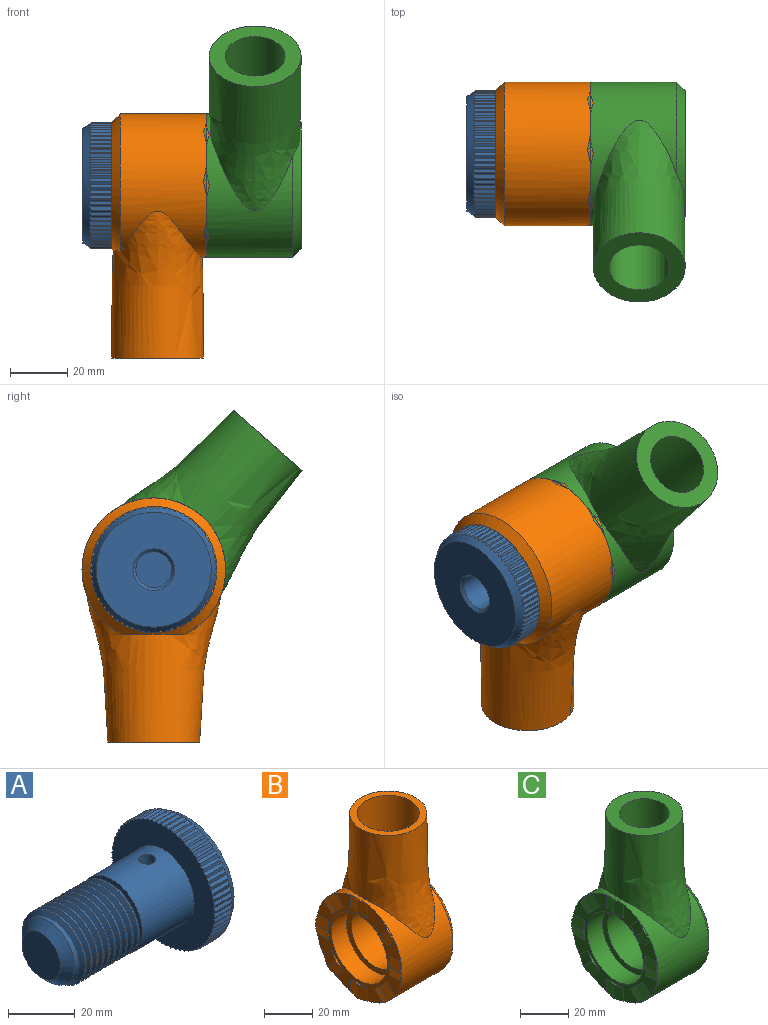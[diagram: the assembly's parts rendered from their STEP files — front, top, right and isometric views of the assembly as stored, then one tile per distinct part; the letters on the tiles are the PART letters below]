
ASSEMBLY  parts=3 mates=2
PART A: 232 faces, bbox 63x45x45 mm
  f0: cylinder r=13mm len=26mm, axis (1,0,0), area 1757.7mm2, adj f223,f224,f230,f231
  f1: cylinder r=6.25mm len=24mm, axis (1,0,0), area 902.3mm2, adj f228,f229,f230,f231
  f2: plane 1.59x1.25mm, normal (0,0,1), area 1.2mm2, adj f4,f6,f17,f224
  f3: bspline ~30.76x26.64mm, area 1329.7mm2, adj f4,f5,f8,f9,f10,f11,f12,f13
  f4: cylinder r=12.75mm len=25.5mm, axis (-1,0,0), area 454mm2, adj f2,f3,f5,f6,f224
  f5: plane 2.49x1.59mm, normal (0,0,-1), area 2.5mm2, adj f3,f4,f6,f7
  f6: bspline ~30.76x26.64mm, area 1376.2mm2, adj f2,f4,f5,f7,f8,f9,f10,f11
  f7: cylinder r=11.16mm len=22.33mm, axis (1,0,0), area 140.6mm2, adj f5,f6,f8,f19
  f8: cylinder r=11.16mm len=22.33mm, axis (1,0,0), area 0.7mm2, adj f3,f6,f7,f9
  f9: cylinder r=11.16mm len=22.33mm, axis (1,0,0), area 0.7mm2, adj f3,f6,f8,f10
  f10: cylinder r=11.16mm len=22.33mm, axis (1,0,0), area 0.8mm2, adj f3,f6,f9,f11
  f11: cylinder r=11.16mm len=22.33mm, axis (1,0,0), area 0.7mm2, adj f3,f6,f10,f12
  f12: cylinder r=11.16mm len=22.33mm, axis (1,0,0), area 0.7mm2, adj f3,f6,f11,f13
  f13: cylinder r=11.16mm len=22.33mm, axis (1,0,0), area 0.6mm2, adj f3,f6,f12,f14
  f14: cylinder r=11.16mm len=22.33mm, axis (1,0,0), area 0.8mm2, adj f3,f6,f13,f15
  f15: cylinder r=11.16mm len=22.33mm, axis (1,0,0), area 0.7mm2, adj f3,f6,f14,f16
  f16: cylinder r=11.16mm len=22.33mm, axis (1,0,0), area 0.7mm2, adj f3,f6,f15,f17
  f17: cylinder r=11.16mm len=22.33mm, axis (1,0,0), area 22.1mm2, adj f2,f3,f16,f224
  f18: plane 16.33x16.33mm, normal (-1,0,0), area 209.4mm2, adj f19
  f19: cone r=11.16mm half-angle=45deg, axis (1,0,0), area 257.6mm2, adj f7,f18
  f20: cylinder r=22mm len=7mm, axis (-1,0,0), area 0.2mm2, adj f21,f223,f225,f227
  f21: plane 7.81x0.97mm, normal (0,0.85,0.53), area 8.3mm2, adj f20,f22,f223,f225
  f22: plane 7.81x1.07mm, normal (0,0.93,-0.36), area 8.3mm2, adj f21,f23,f223,f225
  f23: cylinder r=22mm len=7mm, axis (-1,0,0), area 0.2mm2, adj f22,f24,f223,f225
  f24: plane 7.81x0.91mm, normal (0,0.8,0.6), area 8.3mm2, adj f23,f25,f223,f225
  f25: plane 7.81x1.1mm, normal (0,0.96,-0.28), area 8.3mm2, adj f24,f26,f223,f225
  f26: cylinder r=22mm len=7mm, axis (-1,0,0), area 0.2mm2, adj f25,f27,f223,f225
  f27: plane 7.81x0.85mm, normal (0,0.74,0.67), area 8.3mm2, adj f26,f28,f223,f225
  f28: plane 7.81x1.12mm, normal (0,0.98,-0.19), area 8.3mm2, adj f27,f29,f223,f225
  f29: cylinder r=22mm len=7mm, axis (-1,0,0), area 0.2mm2, adj f28,f30,f223,f225
  f30: plane 7.81x0.85mm, normal (0,0.67,0.74), area 8.3mm2, adj f29,f31,f223,f225
  f31: plane 7.81x1.14mm, normal (0,1,-0.09), area 8.3mm2, adj f30,f32,f223,f225
  f32: cylinder r=22mm len=7mm, axis (-1,0,0), area 0.2mm2, adj f31,f33,f223,f225
  f33: plane 7.81x0.92mm, normal (0,0.6,0.8), area 8.3mm2, adj f32,f34,f223,f225
  f34: plane 7.81x1.14mm, normal (0,1,0), area 8.3mm2, adj f33,f35,f223,f225
  f35: cylinder r=22mm len=7mm, axis (-1,0,0), area 0.2mm2, adj f34,f36,f223,f225
  f36: plane 7.81x0.98mm, normal (0,0.53,0.85), area 8.3mm2, adj f35,f37,f223,f225
  f37: plane 7.81x1.14mm, normal (0,1,0.09), area 8.3mm2, adj f36,f38,f223,f225
  f38: cylinder r=22mm len=7mm, axis (-1,0,0), area 0.2mm2, adj f37,f39,f223,f225
  f39: plane 7.81x1.03mm, normal (0,0.44,0.9), area 8.3mm2, adj f38,f40,f223,f225
  f40: plane 7.81x1.12mm, normal (0,0.98,0.18), area 8.3mm2, adj f39,f41,f223,f225
  f41: cylinder r=22mm len=7mm, axis (-1,0,0), area 0.2mm2, adj f40,f42,f223,f225
  f42: plane 7.81x1.07mm, normal (0,0.36,0.93), area 8.3mm2, adj f41,f43,f223,f225
  f43: plane 7.81x1.1mm, normal (0,0.96,0.27), area 8.3mm2, adj f42,f44,f223,f225
  f44: cylinder r=22mm len=7mm, axis (-1,0,0), area 0.2mm2, adj f43,f45,f223,f225
  f45: plane 7.81x1.1mm, normal (0,0.27,0.96), area 8.3mm2, adj f44,f46,f223,f225
  f46: plane 7.81x1.07mm, normal (0,0.93,0.36), area 8.3mm2, adj f45,f47,f223,f225
  f47: cylinder r=22mm len=7mm, axis (-1,0,0), area 0.2mm2, adj f46,f48,f223,f225
  f48: plane 7.81x1.12mm, normal (0,0.18,0.98), area 8.3mm2, adj f47,f49,f223,f225
  f49: plane 7.81x1.03mm, normal (0,0.9,0.44), area 8.3mm2, adj f48,f50,f223,f225
  f50: cylinder r=22mm len=7mm, axis (-1,0,0), area 0.2mm2, adj f49,f51,f223,f225
  f51: plane 7.81x1.14mm, normal (0,0.09,1), area 8.3mm2, adj f50,f52,f223,f225
  f52: plane 7.81x0.98mm, normal (0,0.85,0.53), area 8.3mm2, adj f51,f53,f223,f225
  f53: cylinder r=22mm len=7mm, axis (-1,0,0), area 0.2mm2, adj f52,f54,f223,f225
  f54: plane 7.81x1.14mm, normal (0,0,1), area 8.3mm2, adj f53,f55,f223,f225
  f55: plane 7.81x0.92mm, normal (0,0.8,0.6), area 8.3mm2, adj f54,f56,f223,f225
  f56: cylinder r=22mm len=7mm, axis (-1,0,0), area 0.2mm2, adj f55,f57,f223,f225
  f57: plane 7.81x1.14mm, normal (0,-0.09,1), area 8.3mm2, adj f56,f58,f223,f225
  f58: plane 7.81x0.85mm, normal (0,0.74,0.67), area 8.3mm2, adj f57,f59,f223,f225
  f59: cylinder r=22mm len=7mm, axis (-1,0,0), area 0.2mm2, adj f58,f60,f223,f225
  f60: plane 7.81x1.12mm, normal (0,-0.19,0.98), area 8.3mm2, adj f59,f61,f223,f225
  f61: plane 7.81x0.85mm, normal (0,0.67,0.74), area 8.3mm2, adj f60,f62,f223,f225
  f62: cylinder r=22mm len=7mm, axis (-1,0,0), area 0.2mm2, adj f61,f63,f223,f225
  f63: plane 7.81x1.1mm, normal (0,-0.28,0.96), area 8.3mm2, adj f62,f64,f223,f225
  f64: plane 7.81x0.91mm, normal (0,0.6,0.8), area 8.3mm2, adj f63,f65,f223,f225
  f65: cylinder r=22mm len=7mm, axis (-1,0,0), area 0.2mm2, adj f64,f66,f223,f225
  f66: plane 7.81x1.07mm, normal (0,-0.36,0.93), area 8.3mm2, adj f65,f67,f223,f225
  f67: plane 7.81x0.97mm, normal (0,0.53,0.85), area 8.3mm2, adj f66,f68,f223,f225
  f68: cylinder r=22mm len=7mm, axis (-1,0,0), area 0.2mm2, adj f67,f69,f223,f225
  f69: plane 7.81x1.02mm, normal (0,-0.45,0.89), area 8.3mm2, adj f68,f70,f223,f225
  f70: plane 7.81x1.02mm, normal (0,0.45,0.89), area 8.3mm2, adj f69,f71,f223,f225
  f71: cylinder r=22mm len=7mm, axis (-1,0,0), area 0.2mm2, adj f70,f72,f223,f225
  f72: plane 7.81x0.97mm, normal (0,-0.53,0.85), area 8.3mm2, adj f71,f73,f223,f225
  f73: plane 7.81x1.07mm, normal (0,0.36,0.93), area 8.3mm2, adj f72,f74,f223,f225
  f74: cylinder r=22mm len=7mm, axis (-1,0,0), area 0.2mm2, adj f73,f75,f223,f225
  f75: plane 7.81x0.91mm, normal (0,-0.6,0.8), area 8.3mm2, adj f74,f76,f223,f225
  f76: plane 7.81x1.1mm, normal (0,0.28,0.96), area 8.3mm2, adj f75,f77,f223,f225
  f77: cylinder r=22mm len=7mm, axis (-1,0,0), area 0.2mm2, adj f76,f78,f223,f225
  f78: plane 7.81x0.85mm, normal (0,-0.67,0.74), area 8.3mm2, adj f77,f79,f223,f225
  f79: plane 7.81x1.12mm, normal (0,0.19,0.98), area 8.3mm2, adj f78,f80,f223,f225
  f80: cylinder r=22mm len=7mm, axis (-1,0,0), area 0.2mm2, adj f79,f81,f223,f225
  f81: plane 7.81x0.85mm, normal (0,-0.74,0.67), area 8.3mm2, adj f80,f82,f223,f225
  f82: plane 7.81x1.14mm, normal (0,0.09,1), area 8.3mm2, adj f81,f83,f223,f225
  f83: cylinder r=22mm len=7mm, axis (-1,0,0), area 0.2mm2, adj f82,f84,f223,f225
  f84: plane 7.81x0.92mm, normal (0,-0.8,0.6), area 8.3mm2, adj f83,f85,f223,f225
  f85: plane 7.81x1.14mm, normal (0,0,1), area 8.3mm2, adj f84,f86,f223,f225
  f86: cylinder r=22mm len=7mm, axis (-1,0,0), area 0.2mm2, adj f85,f87,f223,f225
  f87: plane 7.81x0.98mm, normal (0,-0.85,0.53), area 8.3mm2, adj f86,f88,f223,f225
  f88: plane 7.81x1.14mm, normal (0,-0.09,1), area 8.3mm2, adj f87,f89,f223,f225
  f89: cylinder r=22mm len=7mm, axis (-1,0,0), area 0.2mm2, adj f88,f90,f223,f225
  f90: plane 7.81x1.03mm, normal (0,-0.9,0.44), area 8.3mm2, adj f89,f91,f223,f225
  f91: plane 7.81x1.12mm, normal (0,-0.18,0.98), area 8.3mm2, adj f90,f92,f223,f225
  f92: cylinder r=22mm len=7mm, axis (-1,0,0), area 0.2mm2, adj f91,f93,f223,f225
  f93: plane 7.81x1.07mm, normal (0,-0.93,0.36), area 8.3mm2, adj f92,f94,f223,f225
  f94: plane 7.81x1.1mm, normal (0,-0.27,0.96), area 8.3mm2, adj f93,f95,f223,f225
  f95: cylinder r=22mm len=7mm, axis (-1,0,0), area 0.2mm2, adj f94,f96,f223,f225
  f96: plane 7.81x1.1mm, normal (0,-0.96,0.27), area 8.3mm2, adj f95,f97,f223,f225
  f97: plane 7.81x1.07mm, normal (0,-0.36,0.93), area 8.3mm2, adj f96,f98,f223,f225
  f98: cylinder r=22mm len=7mm, axis (-1,0,0), area 0.2mm2, adj f97,f99,f223,f225
  f99: plane 7.81x1.12mm, normal (0,-0.98,0.18), area 8.3mm2, adj f98,f100,f223,f225
  f100: plane 7.81x1.03mm, normal (0,-0.44,0.9), area 8.3mm2, adj f99,f101,f223,f225
  f101: cylinder r=22mm len=7mm, axis (-1,0,0), area 0.2mm2, adj f100,f102,f223,f225
  f102: plane 7.81x1.14mm, normal (0,-1,0.09), area 8.3mm2, adj f101,f103,f223,f225
  f103: plane 7.81x0.98mm, normal (0,-0.53,0.85), area 8.3mm2, adj f102,f104,f223,f225
  f104: cylinder r=22mm len=7mm, axis (-1,0,0), area 0.2mm2, adj f103,f105,f223,f225
  f105: plane 7.81x1.14mm, normal (0,-1,0), area 8.3mm2, adj f104,f106,f223,f225
  f106: plane 7.81x0.92mm, normal (0,-0.6,0.8), area 8.3mm2, adj f105,f107,f223,f225
  f107: cylinder r=22mm len=7mm, axis (-1,0,0), area 0.2mm2, adj f106,f108,f223,f225
  f108: plane 7.81x1.14mm, normal (0,-1,-0.09), area 8.3mm2, adj f107,f109,f223,f225
  f109: plane 7.81x0.85mm, normal (0,-0.67,0.74), area 8.3mm2, adj f108,f110,f223,f225
  f110: cylinder r=22mm len=7mm, axis (-1,0,0), area 0.2mm2, adj f109,f111,f223,f225
  f111: plane 7.81x1.12mm, normal (0,-0.98,-0.19), area 8.3mm2, adj f110,f112,f223,f225
  f112: plane 7.81x0.85mm, normal (0,-0.74,0.67), area 8.3mm2, adj f111,f113,f223,f225
  f113: cylinder r=22mm len=7mm, axis (-1,0,0), area 0.2mm2, adj f112,f114,f223,f225
  f114: plane 7.81x1.1mm, normal (0,-0.96,-0.28), area 8.3mm2, adj f113,f115,f223,f225
  f115: plane 7.81x0.91mm, normal (0,-0.8,0.6), area 8.3mm2, adj f114,f116,f223,f225
  f116: cylinder r=22mm len=7mm, axis (-1,0,0), area 0.2mm2, adj f115,f117,f223,f225
  f117: plane 7.81x1.07mm, normal (0,-0.93,-0.36), area 8.3mm2, adj f116,f118,f223,f225
  f118: plane 7.81x0.97mm, normal (0,-0.85,0.53), area 8.3mm2, adj f117,f119,f223,f225
  f119: cylinder r=22mm len=7mm, axis (-1,0,0), area 0.2mm2, adj f118,f120,f223,f225
  f120: plane 7.81x1.02mm, normal (0,-0.89,-0.45), area 8.3mm2, adj f119,f121,f223,f225
  f121: plane 7.81x1.02mm, normal (0,-0.89,0.45), area 8.3mm2, adj f120,f122,f223,f225
  f122: cylinder r=22mm len=7mm, axis (-1,0,0), area 0.2mm2, adj f121,f123,f223,f225
  f123: plane 7.81x0.97mm, normal (0,-0.85,-0.53), area 8.3mm2, adj f122,f124,f223,f225
  f124: plane 7.81x1.07mm, normal (0,-0.93,0.36), area 8.3mm2, adj f123,f125,f223,f225
  f125: cylinder r=22mm len=7mm, axis (-1,0,0), area 0.2mm2, adj f124,f126,f223,f225
  f126: plane 7.81x0.91mm, normal (0,-0.8,-0.6), area 8.3mm2, adj f125,f127,f223,f225
  f127: plane 7.81x1.1mm, normal (0,-0.96,0.28), area 8.3mm2, adj f126,f128,f223,f225
  f128: cylinder r=22mm len=7mm, axis (-1,0,0), area 0.2mm2, adj f127,f129,f223,f225
  f129: plane 7.81x0.85mm, normal (0,-0.74,-0.67), area 8.3mm2, adj f128,f130,f223,f225
  f130: plane 7.81x1.12mm, normal (0,-0.98,0.19), area 8.3mm2, adj f129,f131,f223,f225
  f131: cylinder r=22mm len=7mm, axis (-1,0,0), area 0.2mm2, adj f130,f132,f223,f225
  f132: plane 7.81x0.85mm, normal (0,-0.67,-0.74), area 8.3mm2, adj f131,f133,f223,f225
  f133: plane 7.81x1.14mm, normal (0,-1,0.09), area 8.3mm2, adj f132,f134,f223,f225
  f134: cylinder r=22mm len=7mm, axis (-1,0,0), area 0.2mm2, adj f133,f135,f223,f225
  f135: plane 7.81x0.92mm, normal (0,-0.6,-0.8), area 8.3mm2, adj f134,f136,f223,f225
  f136: plane 7.81x1.14mm, normal (0,-1,0), area 8.3mm2, adj f135,f137,f223,f225
  f137: cylinder r=22mm len=7mm, axis (-1,0,0), area 0.2mm2, adj f136,f138,f223,f225
  f138: plane 7.81x0.98mm, normal (0,-0.53,-0.85), area 8.3mm2, adj f137,f139,f223,f225
  f139: plane 7.81x1.14mm, normal (0,-1,-0.09), area 8.3mm2, adj f138,f140,f223,f225
  f140: cylinder r=22mm len=7mm, axis (-1,0,0), area 0.2mm2, adj f139,f141,f223,f225
  f141: plane 7.81x1.03mm, normal (0,-0.44,-0.9), area 8.3mm2, adj f140,f142,f223,f225
  f142: plane 7.81x1.12mm, normal (0,-0.98,-0.18), area 8.3mm2, adj f141,f143,f223,f225
  f143: cylinder r=22mm len=7mm, axis (-1,0,0), area 0.2mm2, adj f142,f144,f223,f225
  f144: plane 7.81x1.07mm, normal (0,-0.36,-0.93), area 8.3mm2, adj f143,f145,f223,f225
  f145: plane 7.81x1.1mm, normal (0,-0.96,-0.27), area 8.3mm2, adj f144,f146,f223,f225
  f146: cylinder r=22mm len=7mm, axis (-1,0,0), area 0.2mm2, adj f145,f147,f223,f225
  f147: plane 7.81x1.1mm, normal (0,-0.27,-0.96), area 8.3mm2, adj f146,f148,f223,f225
  f148: plane 7.81x1.07mm, normal (0,-0.93,-0.36), area 8.3mm2, adj f147,f149,f223,f225
  f149: cylinder r=22mm len=7mm, axis (-1,0,0), area 0.2mm2, adj f148,f150,f223,f225
  f150: plane 7.81x1.12mm, normal (0,-0.18,-0.98), area 8.3mm2, adj f149,f151,f223,f225
  f151: plane 7.81x1.03mm, normal (0,-0.9,-0.44), area 8.3mm2, adj f150,f152,f223,f225
  f152: cylinder r=22mm len=7mm, axis (-1,0,0), area 0.2mm2, adj f151,f153,f223,f225
  f153: plane 7.81x1.14mm, normal (0,-0.09,-1), area 8.3mm2, adj f152,f154,f223,f225
  f154: plane 7.81x0.98mm, normal (0,-0.85,-0.53), area 8.3mm2, adj f153,f155,f223,f225
  f155: cylinder r=22mm len=7mm, axis (-1,0,0), area 0.2mm2, adj f154,f156,f223,f225
  f156: plane 7.81x1.14mm, normal (0,0,-1), area 8.3mm2, adj f155,f157,f223,f225
  f157: plane 7.81x0.92mm, normal (0,-0.8,-0.6), area 8.3mm2, adj f156,f158,f223,f225
  f158: cylinder r=22mm len=7mm, axis (-1,0,0), area 0.2mm2, adj f157,f159,f223,f225
  f159: plane 7.81x1.14mm, normal (0,0.09,-1), area 8.3mm2, adj f158,f160,f223,f225
  f160: plane 7.81x0.85mm, normal (0,-0.74,-0.67), area 8.3mm2, adj f159,f161,f223,f225
  f161: cylinder r=22mm len=7mm, axis (-1,0,0), area 0.2mm2, adj f160,f162,f223,f225
  f162: plane 7.81x1.12mm, normal (0,0.19,-0.98), area 8.3mm2, adj f161,f163,f223,f225
  f163: plane 7.81x0.85mm, normal (0,-0.67,-0.74), area 8.3mm2, adj f162,f164,f223,f225
  f164: cylinder r=22mm len=7mm, axis (-1,0,0), area 0.2mm2, adj f163,f165,f223,f225
  f165: plane 7.81x1.1mm, normal (0,0.28,-0.96), area 8.3mm2, adj f164,f166,f223,f225
  f166: plane 7.81x0.91mm, normal (0,-0.6,-0.8), area 8.3mm2, adj f165,f167,f223,f225
  f167: cylinder r=22mm len=7mm, axis (-1,0,0), area 0.2mm2, adj f166,f168,f223,f225
  f168: plane 7.81x1.07mm, normal (0,0.36,-0.93), area 8.3mm2, adj f167,f169,f223,f225
  f169: plane 7.81x0.97mm, normal (0,-0.53,-0.85), area 8.3mm2, adj f168,f170,f223,f225
  f170: cylinder r=22mm len=7mm, axis (-1,0,0), area 0.2mm2, adj f169,f171,f223,f225
  f171: plane 7.81x1.02mm, normal (0,0.45,-0.89), area 8.3mm2, adj f170,f172,f223,f225
  f172: plane 7.81x1.02mm, normal (0,-0.45,-0.89), area 8.3mm2, adj f171,f173,f223,f225
  f173: cylinder r=22mm len=7mm, axis (-1,0,0), area 0.2mm2, adj f172,f174,f223,f225
  f174: plane 7.81x0.97mm, normal (0,0.53,-0.85), area 8.3mm2, adj f173,f175,f223,f225
  f175: plane 7.81x1.07mm, normal (0,-0.36,-0.93), area 8.3mm2, adj f174,f176,f223,f225
  f176: cylinder r=22mm len=7mm, axis (-1,0,0), area 0.2mm2, adj f175,f177,f223,f225
  f177: plane 7.81x0.91mm, normal (0,0.6,-0.8), area 8.3mm2, adj f176,f178,f223,f225
  f178: plane 7.81x1.1mm, normal (0,-0.28,-0.96), area 8.3mm2, adj f177,f179,f223,f225
  f179: cylinder r=22mm len=7mm, axis (-1,0,0), area 0.2mm2, adj f178,f180,f223,f225
  f180: plane 7.81x0.85mm, normal (0,0.67,-0.74), area 8.3mm2, adj f179,f181,f223,f225
  f181: plane 7.81x1.12mm, normal (0,-0.19,-0.98), area 8.3mm2, adj f180,f182,f223,f225
  f182: cylinder r=22mm len=7mm, axis (-1,0,0), area 0.2mm2, adj f181,f183,f223,f225
  f183: plane 7.81x0.85mm, normal (0,0.74,-0.67), area 8.3mm2, adj f182,f184,f223,f225
  f184: plane 7.81x1.14mm, normal (0,-0.09,-1), area 8.3mm2, adj f183,f185,f223,f225
  f185: cylinder r=22mm len=7mm, axis (-1,0,0), area 0.2mm2, adj f184,f186,f223,f225
  f186: plane 7.81x0.92mm, normal (0,0.8,-0.6), area 8.3mm2, adj f185,f187,f223,f225
  f187: plane 7.81x1.14mm, normal (0,0,-1), area 8.3mm2, adj f186,f188,f223,f225
  f188: cylinder r=22mm len=7mm, axis (-1,0,0), area 0.2mm2, adj f187,f189,f223,f225
  f189: plane 7.81x0.98mm, normal (0,0.85,-0.53), area 8.3mm2, adj f188,f190,f223,f225
  f190: plane 7.81x1.14mm, normal (0,0.09,-1), area 8.3mm2, adj f189,f191,f223,f225
  f191: cylinder r=22mm len=7mm, axis (-1,0,0), area 0.2mm2, adj f190,f192,f223,f225
  f192: plane 7.81x1.03mm, normal (0,0.9,-0.44), area 8.3mm2, adj f191,f193,f223,f225
  f193: plane 7.81x1.12mm, normal (0,0.18,-0.98), area 8.3mm2, adj f192,f194,f223,f225
  f194: cylinder r=22mm len=7mm, axis (-1,0,0), area 0.2mm2, adj f193,f195,f223,f225
  f195: plane 7.81x1.07mm, normal (0,0.93,-0.36), area 8.3mm2, adj f194,f196,f223,f225
  f196: plane 7.81x1.1mm, normal (0,0.27,-0.96), area 8.3mm2, adj f195,f197,f223,f225
  f197: cylinder r=22mm len=7mm, axis (-1,0,0), area 0.2mm2, adj f196,f198,f223,f225
  f198: plane 7.81x1.1mm, normal (0,0.96,-0.27), area 8.3mm2, adj f197,f199,f223,f225
  f199: plane 7.81x1.07mm, normal (0,0.36,-0.93), area 8.3mm2, adj f198,f200,f223,f225
  f200: cylinder r=22mm len=7mm, axis (-1,0,0), area 0.2mm2, adj f199,f201,f223,f225
  f201: plane 7.81x1.12mm, normal (0,0.98,-0.18), area 8.3mm2, adj f200,f202,f223,f225
  f202: plane 7.81x1.03mm, normal (0,0.44,-0.9), area 8.3mm2, adj f201,f203,f223,f225
  f203: cylinder r=22mm len=7mm, axis (-1,0,0), area 0.2mm2, adj f202,f204,f223,f225
  f204: plane 7.81x1.14mm, normal (0,1,-0.09), area 8.3mm2, adj f203,f205,f223,f225
  f205: plane 7.81x0.98mm, normal (0,0.53,-0.85), area 8.3mm2, adj f204,f206,f223,f225
  f206: cylinder r=22mm len=7mm, axis (-1,0,0), area 0.2mm2, adj f205,f207,f223,f225
  f207: plane 7.81x1.14mm, normal (0,1,0), area 8.3mm2, adj f206,f208,f223,f225
  f208: plane 7.81x0.92mm, normal (0,0.6,-0.8), area 8.3mm2, adj f207,f209,f223,f225
  f209: cylinder r=22mm len=7mm, axis (-1,0,0), area 0.2mm2, adj f208,f210,f223,f225
  f210: plane 7.81x1.14mm, normal (0,1,0.09), area 8.3mm2, adj f209,f211,f223,f225
  f211: plane 7.81x0.85mm, normal (0,0.67,-0.74), area 8.3mm2, adj f210,f212,f223,f225
  f212: cylinder r=22mm len=7mm, axis (-1,0,0), area 0.2mm2, adj f211,f213,f223,f225
  f213: plane 7.81x1.12mm, normal (0,0.98,0.19), area 8.3mm2, adj f212,f214,f223,f225
  f214: plane 7.81x0.85mm, normal (0,0.74,-0.67), area 8.3mm2, adj f213,f215,f223,f225
  f215: cylinder r=22mm len=7mm, axis (-1,0,0), area 0.2mm2, adj f214,f216,f223,f225
  f216: plane 7.81x1.1mm, normal (0,0.96,0.28), area 8.3mm2, adj f215,f217,f223,f225
  f217: plane 7.81x0.91mm, normal (0,0.8,-0.6), area 8.3mm2, adj f216,f218,f223,f225
  f218: cylinder r=22mm len=7mm, axis (-1,0,0), area 0.2mm2, adj f217,f219,f223,f225
  f219: plane 7.81x1.07mm, normal (0,0.93,0.36), area 8.3mm2, adj f218,f220,f223,f225
  f220: plane 7.81x0.97mm, normal (0,0.85,-0.53), area 8.3mm2, adj f219,f221,f223,f225
  f221: cylinder r=22mm len=7mm, axis (-1,0,0), area 0.2mm2, adj f220,f223,f225,f226
  f222: plane 40x40mm, normal (1,0,0), area 1091.5mm2, adj f225,f229
  f223: plane 43.95x43.95mm, normal (-1,0,0), area 953.5mm2, adj f0,f20,f21,f22,f23,f24,f25,f26
  f224: plane 26.99x26.99mm, normal (-1,0,0), area 102.4mm2, adj f0,f2,f3,f4,f17
  f225: cone r=20mm half-angle=33.7deg, axis (-1,0,0), area 412.1mm2, adj f20,f21,f22,f23,f24,f25,f26,f27
  f226: plane 7.81x1.02mm, normal (0,0.89,0.45), area 8.3mm2, adj f221,f223,f225,f227
  f227: plane 7.81x1.02mm, normal (0,0.89,-0.45), area 8.3mm2, adj f20,f223,f225,f226
  f228: plane 12.5x12.5mm, normal (1,0,0), area 122.7mm2, adj f1
  f229: cone r=6.25mm half-angle=45deg, axis (1,0,0), area 60mm2, adj f1,f222
  f230: cylinder r=2.5mm len=6.75mm, axis (0,0,-1), area 106mm2, adj f0,f1
  f231: cylinder r=2.5mm len=6.75mm, axis (0,0,-1), area 106mm2, adj f0,f1
PART B: 43 faces, bbox 35x51x86 mm
  f0: extruded ~7.07x7.07mm, area 5mm2, adj f1,f2,f29
  f1: plane 8.49x8.13mm, normal (-0.98,0.14,0.14), area 34.8mm2, adj f0,f2,f3,f28
  f2: plane 8.49x8.13mm, normal (-0.98,-0.14,-0.14), area 34.8mm2, adj f0,f1,f3,f28
  f3: plane 7.07x7.07mm, normal (0,0.71,-0.71), area 5mm2, adj f1,f2,f28
  f4: extruded ~10x1mm, area 5mm2, adj f5,f6,f29
  f5: plane 7.01x5.01mm, normal (-0.98,0.2,0), area 34.8mm2, adj f4,f6,f7,f28
  f6: plane 7.01x5.01mm, normal (-0.98,-0.2,0), area 34.8mm2, adj f4,f5,f7,f28
  f7: plane 10x1mm, normal (0,0,-1), area 5mm2, adj f5,f6,f28
  f8: extruded ~7.07x7.07mm, area 5mm2, adj f9,f10,f29
  f9: plane 8.49x8.13mm, normal (-0.98,0.14,-0.14), area 34.8mm2, adj f8,f10,f11,f28
  f10: plane 8.49x8.13mm, normal (-0.98,-0.14,0.14), area 34.8mm2, adj f8,f9,f11,f28
  f11: plane 7.07x7.07mm, normal (0,-0.71,-0.71), area 5mm2, adj f9,f10,f28
  f12: extruded ~10x1mm, area 5mm2, adj f13,f14,f29
  f13: plane 7.01x5.01mm, normal (-0.98,0,-0.2), area 34.8mm2, adj f12,f14,f15,f28
  f14: plane 7.01x5.01mm, normal (-0.98,0,0.2), area 34.8mm2, adj f12,f13,f15,f28
  f15: plane 10x1mm, normal (0,-1,0), area 5mm2, adj f13,f14,f28
  f16: extruded ~7.07x7.07mm, area 5mm2, adj f17,f18,f29
  f17: plane 8.49x8.13mm, normal (-0.98,-0.14,-0.14), area 34.8mm2, adj f16,f18,f19,f28
  f18: plane 8.49x8.13mm, normal (-0.98,0.14,0.14), area 34.8mm2, adj f16,f17,f19,f28
  f19: plane 7.07x7.07mm, normal (0,-0.71,0.71), area 5mm2, adj f17,f18,f28
  f20: extruded ~10x1mm, area 5mm2, adj f21,f22,f29
  f21: plane 7.01x5.01mm, normal (-0.98,-0.2,0), area 34.8mm2, adj f20,f22,f23,f28
  f22: plane 7.01x5.01mm, normal (-0.98,0.2,0), area 34.8mm2, adj f20,f21,f23,f28
  f23: plane 10x1mm, normal (0,0,1), area 5mm2, adj f21,f22,f28
  f24: extruded ~7.07x7.07mm, area 5mm2, adj f25,f26,f29
  f25: plane 8.49x8.13mm, normal (-0.98,-0.14,0.14), area 34.8mm2, adj f24,f26,f27,f28
  f26: plane 8.49x8.13mm, normal (-0.98,0.14,-0.14), area 34.8mm2, adj f24,f25,f27,f28
  f27: plane 7.07x7.07mm, normal (0,0.71,0.71), area 5mm2, adj f25,f26,f28
  f28: plane 48.99x48.99mm, normal (-1,0,0), area 561.6mm2, adj f1,f2,f3,f5,f6,f7,f9,f10
  f29: cylinder r=25mm len=50mm, axis (-1,0,0), area 3468mm2, adj f0,f4,f8,f12,f16,f20,f24,f28
  f30: plane 44x44mm, normal (1,0,0), area 926.6mm2, adj f33,f42
  f31: bspline ~51.49x46.75mm, area 4323.7mm2, adj f29,f32,f33
  f32: plane 32.98x32.98mm, normal (0,0,1), area 281.4mm2, adj f31,f38
  f33: cone r=22mm half-angle=45deg, axis (-1,0,0), area 577.6mm2, adj f29,f30,f31
  f34: plane 7.01x5.01mm, normal (-0.98,0,0.2), area 34.8mm2, adj f28,f35,f36,f37
  f35: plane 7.01x5.01mm, normal (-0.98,0,-0.2), area 34.8mm2, adj f28,f34,f36,f37
  f36: plane 10x1mm, normal (0,1,0), area 5mm2, adj f28,f34,f35
  f37: extruded ~10x1mm, area 5mm2, adj f29,f34,f35
  f38: cylinder r=12.9mm len=30mm, axis (0,0,1), area 2431.6mm2, adj f32,f39
  f39: plane 25.8x25.8mm, normal (0,0,1), area 522.8mm2, adj f38
  f40: cylinder r=16.5mm len=33mm, axis (-1,0,0), area 933.1mm2, adj f28,f41
  f41: plane 33x33mm, normal (-1,0,0), area 261.3mm2, adj f40,f42
  f42: cylinder r=13.75mm len=27.5mm, axis (-1,0,0), area 2073.5mm2, adj f30,f41
PART C: 43 faces, bbox 35x51x86 mm
  f0: extruded ~7.07x7.07mm, area 5mm2, adj f1,f2,f29
  f1: plane 8.49x8.13mm, normal (-0.98,0.14,0.14), area 34.8mm2, adj f0,f2,f3,f28
  f2: plane 8.49x8.13mm, normal (-0.98,-0.14,-0.14), area 34.8mm2, adj f0,f1,f3,f28
  f3: plane 7.07x7.07mm, normal (0,0.71,-0.71), area 5mm2, adj f1,f2,f28
  f4: extruded ~10x1mm, area 5mm2, adj f5,f6,f29
  f5: plane 7.01x5.01mm, normal (-0.98,0.2,0), area 34.8mm2, adj f4,f6,f7,f28
  f6: plane 7.01x5.01mm, normal (-0.98,-0.2,0), area 34.8mm2, adj f4,f5,f7,f28
  f7: plane 10x1mm, normal (0,0,-1), area 5mm2, adj f5,f6,f28
  f8: extruded ~7.07x7.07mm, area 5mm2, adj f9,f10,f29
  f9: plane 8.49x8.13mm, normal (-0.98,0.14,-0.14), area 34.8mm2, adj f8,f10,f11,f28
  f10: plane 8.49x8.13mm, normal (-0.98,-0.14,0.14), area 34.8mm2, adj f8,f9,f11,f28
  f11: plane 7.07x7.07mm, normal (0,-0.71,-0.71), area 5mm2, adj f9,f10,f28
  f12: extruded ~10x1mm, area 5mm2, adj f13,f14,f29
  f13: plane 7.01x5.01mm, normal (-0.98,0,-0.2), area 34.8mm2, adj f12,f14,f15,f28
  f14: plane 7.01x5.01mm, normal (-0.98,0,0.2), area 34.8mm2, adj f12,f13,f15,f28
  f15: plane 10x1mm, normal (0,-1,0), area 5mm2, adj f13,f14,f28
  f16: extruded ~7.07x7.07mm, area 5mm2, adj f17,f18,f29
  f17: plane 8.49x8.13mm, normal (-0.98,-0.14,-0.14), area 34.8mm2, adj f16,f18,f19,f28
  f18: plane 8.49x8.13mm, normal (-0.98,0.14,0.14), area 34.8mm2, adj f16,f17,f19,f28
  f19: plane 7.07x7.07mm, normal (0,-0.71,0.71), area 5mm2, adj f17,f18,f28
  f20: extruded ~10x1mm, area 5mm2, adj f21,f22,f29
  f21: plane 7.01x5.01mm, normal (-0.98,-0.2,0), area 34.8mm2, adj f20,f22,f23,f28
  f22: plane 7.01x5.01mm, normal (-0.98,0.2,0), area 34.8mm2, adj f20,f21,f23,f28
  f23: plane 10x1mm, normal (0,0,1), area 5mm2, adj f21,f22,f28
  f24: extruded ~7.07x7.07mm, area 5mm2, adj f25,f26,f29
  f25: plane 8.49x8.13mm, normal (-0.98,-0.14,0.14), area 34.8mm2, adj f24,f26,f27,f28
  f26: plane 8.49x8.13mm, normal (-0.98,0.14,-0.14), area 34.8mm2, adj f24,f25,f27,f28
  f27: plane 7.07x7.07mm, normal (0,0.71,0.71), area 5mm2, adj f25,f26,f28
  f28: plane 48.99x48.99mm, normal (-1,0,0), area 561.6mm2, adj f1,f2,f3,f5,f6,f7,f9,f10
  f29: cylinder r=25mm len=50mm, axis (-1,0,0), area 3468mm2, adj f0,f4,f8,f12,f16,f20,f24,f28
  f30: plane 44x44mm, normal (1,0,0), area 926.6mm2, adj f33,f42
  f31: bspline ~51.49x46.75mm, area 4323.7mm2, adj f29,f32,f33
  f32: plane 32.98x32.98mm, normal (0,0,1), area 464.4mm2, adj f31,f38
  f33: cone r=22mm half-angle=45deg, axis (-1,0,0), area 577.6mm2, adj f29,f30,f31
  f34: plane 7.01x5.01mm, normal (-0.98,0,0.2), area 34.8mm2, adj f28,f35,f36,f37
  f35: plane 7.01x5.01mm, normal (-0.98,0,-0.2), area 34.8mm2, adj f28,f34,f36,f37
  f36: plane 10x1mm, normal (0,1,0), area 5mm2, adj f28,f34,f35
  f37: extruded ~10x1mm, area 5mm2, adj f29,f34,f35
  f38: cylinder r=10.4mm len=30mm, axis (0,0,1), area 1960.4mm2, adj f32,f39
  f39: plane 20.8x20.8mm, normal (0,0,1), area 339.8mm2, adj f38
  f40: cylinder r=16.5mm len=33mm, axis (-1,0,0), area 933.1mm2, adj f28,f41
  f41: plane 33x33mm, normal (-1,0,0), area 261.3mm2, adj f40,f42
  f42: cylinder r=13.75mm len=27.5mm, axis (-1,0,0), area 2073.5mm2, adj f30,f41
PLACE A rot(axis=(0,-0.78,-0.63),180deg) t=(0,0,1.4)mm
PLACE B rot(axis=(0,1,0),180deg) t=(0,0,1.4)mm fixed
PLACE C rot(axis=(1,0,0),41.3deg) t=(0,0,1.4)mm
MATE revolute A.f20 <-> B.f29  axis (1,0,0) through (-33,0,1.4)mm
MATE revolute B.f29 <-> C.f29  axis (1,0,0) through (0,0,1.4)mm
